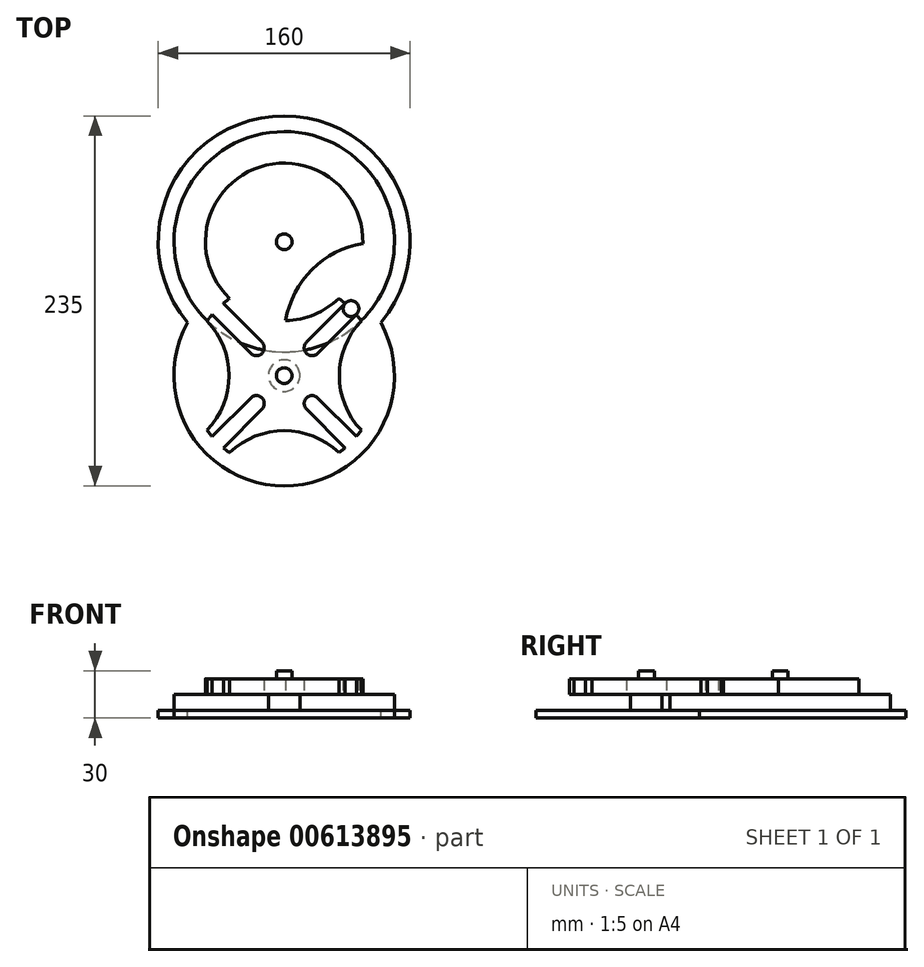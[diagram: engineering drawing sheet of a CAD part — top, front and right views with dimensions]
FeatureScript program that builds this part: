
annotation { "Feature Type Name" : "Feature", "Feature Type Description" : "" }
export const myFeature = defineFeature(function(context is Context, id is Id, definition is map)
    precondition{}
    {
        {
            var Q0;
            Q0=qCreatedBy(makeId("Top.planeOp"),FACE);
            cPlane(context, id + "F0", {"entities" : qUnion([Q0]), "cplaneType" : CPlaneType.OFFSET, "offset" : 10 * mm, "oppositeDirection" : true, "width" : 150 * mm, "height" : 150 * mm});
        }
        {
            var Q0;
            Q0=qCreatedBy(makeId("Top.planeOp"),FACE);
            var sketch = newSketch(context, id + "F1", { "sketchPlane" : qUnion([Q0])});
            skCircle(sketch, "E0", {"center": v(0, 0) * mm, "radius": 70 * mm});
            skCircle(sketch, "E1", {"center": v(0, -60) * mm, "radius": 5 * mm});
            skLineSegment(sketch, "E2", {"start": v(0, -50) * mm, "end": v(0, -70) * mm, "construction": true});
            skCircle(sketch, "E3", {"center": v(0, 0) * mm, "radius": 5 * mm});
            skArc(sketch, "E4", {"start": v(48.84, -50.15) * mm, "mid": v(42.35, -42.5) * mm, "end": v(34.67, -36.03) * mm, "construction": true});
            skArc(sketch, "E5", {"start": v(-48.84, -50.15) * mm, "mid": v(0, -145) * mm, "end": v(48.84, -50.15) * mm, "construction": true});
            skArc(sketch, "E6", {"start": v(-34.67, -36.03) * mm, "mid": v(-42.35, -42.5) * mm, "end": v(-48.84, -50.15) * mm, "construction": true});
            skArc(sketch, "E7", {"start": v(34.67, -36.03) * mm, "mid": v(0, -25) * mm, "end": v(-34.67, -36.03) * mm});
            skArc(sketch, "E8", {"start": v(34.67, -36.03) * mm, "mid": v(0, 50) * mm, "end": v(-34.67, -36.03) * mm});
            skArc(sketch, "E9", {"start": v(-34.67, -36.03) * mm, "mid": v(0, -50) * mm, "end": v(34.67, -36.03) * mm, "construction": true});
            skSolve(sketch);
        }
        {
            var Q0;
            Q0=makeQuery(id+"F1.imprint","IMPRINT",FACE,{"disambiguationData":[TD([[makeQuery(id+"F1.imprint","IMPRINT",EDGE,{"derivedFrom":sQuery(id+"F1.wireOp",EDGE,"E0")}),1.0]])]});
            var Q1;
            Q1=makeQuery(id+"F1.imprint","IMPRINT",FACE,{"disambiguationData":[TD([[makeQuery(id+"F1.imprint","IMPRINT",EDGE,{"derivedFrom":sQuery(id+"F1.wireOp",EDGE,"E3")}),-1.0]])]});
            var Q2;
            Q2=makeQuery(id+"F1.imprint","IMPRINT",FACE,{"disambiguationData":[TD([[makeQuery(id+"F1.imprint","IMPRINT",EDGE,{"derivedFrom":sQuery(id+"F1.wireOp",EDGE,"E1")}),1.0]])]});
            var Q3;
            Q3=qCreatedBy(id+"F0.planeOp",FACE);
            extrude(context, id + "F2", {"entities" : qUnion([Q0, Q1, Q2]), "endBound" : BoundingType.UP_TO_SURFACE, "oppositeDirection" : true, "depth" : 5 * mm, "endBoundEntityFace" : qUnion([Q3]), "offsetDistance" : 25 * mm});
        }
        {
            var Q0;
            Q0=makeQuery(id+"F1.imprint","IMPRINT",FACE,{"disambiguationData":[TD([[makeQuery(id+"F1.imprint","IMPRINT",EDGE,{"derivedFrom":sQuery(id+"F1.wireOp",EDGE,"E3")}),-1.0]])]});
            var Q1;
            Q1=makeQuery(id+"F1.imprint","IMPRINT",FACE,{"disambiguationData":[TD([[makeQuery(id+"F1.imprint","IMPRINT",EDGE,{"derivedFrom":sQuery(id+"F1.wireOp",EDGE,"E1")}),1.0]])]});
            extrude(context, id + "F3", {"entities" : qUnion([Q0, Q1]), "operationType" : NewBodyOperationType.ADD, "depth" : 10 * mm, "offsetDistance" : 25 * mm});
        }
        {
            var Q0;
            Q0=makeQuery(id+"F2.opExtrude","SWEPT_BODY",BODY,{"disambiguationData":[OSD([sQuery(id+"F1.wireOp",EDGE,"E0"),sQuery(id+"F1.wireOp",EDGE,"E3")])]});
            var Q1;
            Q1=makeQuery(id+"F3.opExtrude","CAP_EDGE",EDGE,{"disambiguationData":[OSD([sQuery(id+"F1.wireOp",EDGE,"E3")])],"isStart":false});
            transform(context, id + "F4", {"entities" : qUnion([Q0]), "transformType" : TransformType.ROTATION, "transformAxis" : qUnion([Q1]), "angle" : 45 * degree, "makeCopy" : false});
        }
        {
            var Q0;
            Q0=qCreatedBy(makeId("Top.planeOp"),FACE);
            var sketch = newSketch(context, id + "F5", { "sketchPlane" : qUnion([Q0])});
            skPoint(sketch, "E10.0", {"position": v(0, -85) * mm});
            skLineSegment(sketch, "E11", {"start": v(38.66, -39.12) * mm, "end": v(38.66, -39.12) * mm});
            skArc(sketch, "E12.0", {"start": v(-34.67, -36.03) * mm, "mid": v(0, -50) * mm, "end": v(34.67, -36.03) * mm});
            skLineSegment(sketch, "E13", {"start": v(0, -85) * mm, "end": v(14.14, -70.86) * mm, "construction": true});
            skLineSegment(sketch, "E14", {"start": v(-3.54, -81.46) * mm, "end": v(-42.43, -42.57) * mm, "construction": true});
            skCircle(sketch, "E15.0.0", {"center": v(42.43, -42.43) * mm, "radius": 5 * mm, "construction": true});
            skArc(sketch, "E16", {"start": v(0, -60) * mm, "mid": v(7.2, -61.06) * mm, "end": v(13.8, -64.16) * mm, "construction": true});
            skArc(sketch, "E17", {"start": v(14.13, -63.8) * mm, "mid": v(12.68, -67.33) * mm, "end": v(14.14, -70.86) * mm});
            skLineSegment(sketch, "E18", {"start": v(38.66, -39.12) * mm, "end": v(14.13, -63.8) * mm});
            skArc(sketch, "E19", {"start": v(34.67, -36.03) * mm, "mid": v(-5.07, -25.22) * mm, "end": v(-42.43, -42.57) * mm, "construction": true});
            skArc(sketch, "E20", {"start": v(38.66, -39.12) * mm, "mid": v(36.7, -37.53) * mm, "end": v(34.67, -36.03) * mm});
            skArc(sketch, "E21.MirrorCS", {"start": v(-38.66, -39.12) * mm, "mid": v(-36.7, -37.53) * mm, "end": v(-34.67, -36.03) * mm});
            skLineSegment(sketch, "E22.MirrorCS", {"start": v(0, -85) * mm, "end": v(-14.14, -70.86) * mm, "construction": true});
            skLineSegment(sketch, "E23.MirrorCS", {"start": v(-38.66, -39.12) * mm, "end": v(-14.13, -63.8) * mm});
            skArc(sketch, "E24.MirrorCS", {"start": v(-14.13, -63.8) * mm, "mid": v(-12.68, -67.33) * mm, "end": v(-14.14, -70.86) * mm});
            skArc(sketch, "E25.1.0", {"start": v(-21.2, -70.87) * mm, "mid": v(-17.67, -72.32) * mm, "end": v(-14.14, -70.86) * mm});
            skLineSegment(sketch, "E25.1.1", {"start": v(-45.88, -46.34) * mm, "end": v(-21.2, -70.87) * mm});
            skLineSegment(sketch, "E25.1.2", {"start": v(0, -85) * mm, "end": v(-14.14, -70.86) * mm});
            skArc(sketch, "E25.1.3", {"start": v(-48.97, -119.67) * mm, "mid": v(-35, -85) * mm, "end": v(-48.97, -50.33) * mm});
            skLineSegment(sketch, "E25.1.4", {"start": v(-45.88, -123.66) * mm, "end": v(-21.2, -99.13) * mm});
            skArc(sketch, "E25.1.5", {"start": v(-21.2, -99.13) * mm, "mid": v(-17.67, -97.68) * mm, "end": v(-14.14, -99.14) * mm});
            skLineSegment(sketch, "E25.1.6", {"start": v(0, -85) * mm, "end": v(-14.14, -99.14) * mm, "construction": true});
            skArc(sketch, "E25.1.9", {"start": v(-45.88, -46.34) * mm, "mid": v(-47.47, -48.3) * mm, "end": v(-48.97, -50.33) * mm});
            skArc(sketch, "E25.1.10", {"start": v(-45.88, -123.66) * mm, "mid": v(-47.47, -121.7) * mm, "end": v(-48.97, -119.67) * mm});
            skArc(sketch, "E25.2.0", {"start": v(-14.13, -106.2) * mm, "mid": v(-12.68, -102.67) * mm, "end": v(-14.14, -99.14) * mm});
            skLineSegment(sketch, "E25.2.1", {"start": v(-38.66, -130.88) * mm, "end": v(-14.13, -106.2) * mm});
            skLineSegment(sketch, "E25.2.2", {"start": v(-3.54, -88.54) * mm, "end": v(-14.14, -99.14) * mm});
            skArc(sketch, "E25.2.3", {"start": v(34.67, -133.97) * mm, "mid": v(0, -120) * mm, "end": v(-34.67, -133.97) * mm});
            skLineSegment(sketch, "E25.2.4", {"start": v(38.66, -130.88) * mm, "end": v(14.13, -106.2) * mm});
            skArc(sketch, "E25.2.5", {"start": v(14.13, -106.2) * mm, "mid": v(12.68, -102.67) * mm, "end": v(14.14, -99.14) * mm});
            skLineSegment(sketch, "E25.2.6", {"start": v(0, -85) * mm, "end": v(14.14, -99.14) * mm, "construction": true});
            skArc(sketch, "E25.2.9", {"start": v(-38.66, -130.88) * mm, "mid": v(-36.7, -132.47) * mm, "end": v(-34.67, -133.97) * mm});
            skArc(sketch, "E25.2.10", {"start": v(38.66, -130.88) * mm, "mid": v(36.7, -132.47) * mm, "end": v(34.67, -133.97) * mm});
            skArc(sketch, "E25.3.0", {"start": v(21.2, -99.13) * mm, "mid": v(17.67, -97.68) * mm, "end": v(14.14, -99.14) * mm});
            skLineSegment(sketch, "E25.3.1", {"start": v(45.88, -123.66) * mm, "end": v(21.2, -99.13) * mm});
            skLineSegment(sketch, "E25.3.2", {"start": v(3.54, -88.54) * mm, "end": v(14.14, -99.14) * mm});
            skArc(sketch, "E25.3.3", {"start": v(48.97, -50.33) * mm, "mid": v(35, -85) * mm, "end": v(48.97, -119.67) * mm});
            skLineSegment(sketch, "E25.3.4", {"start": v(45.88, -46.34) * mm, "end": v(21.2, -70.87) * mm});
            skArc(sketch, "E25.3.5", {"start": v(21.2, -70.87) * mm, "mid": v(17.67, -72.32) * mm, "end": v(14.14, -70.86) * mm});
            skLineSegment(sketch, "E25.3.6", {"start": v(3.54, -81.46) * mm, "end": v(14.14, -70.86) * mm});
            skArc(sketch, "E25.3.9", {"start": v(45.88, -123.66) * mm, "mid": v(47.47, -121.7) * mm, "end": v(48.97, -119.67) * mm});
            skArc(sketch, "E25.3.10", {"start": v(45.88, -46.34) * mm, "mid": v(47.47, -48.3) * mm, "end": v(48.97, -50.33) * mm});
            skCircle(sketch, "E26", {"center": v(0, -85) * mm, "radius": 5 * mm});
            skCircle(sketch, "E27", {"center": v(0, -85) * mm, "radius": 10 * mm});
            skSolve(sketch);
        }
        {
            var Q0;
            Q0 = qSketchRegion(id + "F5", true);
            var Q1;
            {var subQ0=sQuery(id+"F5.wireOp",EDGE,"E26");var subQ1=sQuery(id+"F5.wireOp",EDGE,"E25.1.2");var subQ2=makeQuery(id+"F5.imprint","INTERSECT",VERTEX,{"derivedFrom":[subQ1,subQ0]});Q1=makeQuery(id+"F5.imprint","IMPRINT",FACE,{"disambiguationData":[TD([[makeQuery(id+"F5.imprint","IMPRINT",EDGE,{"disambiguationData":[TD([[subQ2,-1.0]])],"derivedFrom":subQ1}),1.0]])]});}
            var Q2;
            {var subQ0=sQuery(id+"F5.wireOp",EDGE,"E26");var subQ1=sQuery(id+"F5.wireOp",EDGE,"E25.1.2");var subQ2=makeQuery(id+"F5.imprint","INTERSECT",VERTEX,{"derivedFrom":[subQ1,subQ0]});Q2=makeQuery(id+"F5.imprint","IMPRINT",FACE,{"disambiguationData":[TD([[makeQuery(id+"F5.imprint","IMPRINT",EDGE,{"disambiguationData":[TD([[subQ2,-1.0]])],"derivedFrom":subQ1}),-1.0]])]});}
            var Q3;
            {var subQ0=sQuery(id+"F5.wireOp",EDGE,"E26");var subQ1=sQuery(id+"F5.wireOp",EDGE,"E25.3.2");var subQ2=makeQuery(id+"F5.imprint","INTERSECT",VERTEX,{"derivedFrom":[subQ1,subQ0]});Q3=makeQuery(id+"F5.imprint","IMPRINT",FACE,{"disambiguationData":[TD([[makeQuery(id+"F5.imprint","IMPRINT",EDGE,{"disambiguationData":[TD([[subQ2,-1.0]])],"derivedFrom":subQ1}),1.0]])]});}
            var Q4;
            {var subQ0=sQuery(id+"F5.wireOp",EDGE,"E26");var subQ1=sQuery(id+"F5.wireOp",EDGE,"E25.2.2");var subQ2=makeQuery(id+"F5.imprint","INTERSECT",VERTEX,{"derivedFrom":[subQ1,subQ0]});Q4=makeQuery(id+"F5.imprint","IMPRINT",FACE,{"disambiguationData":[TD([[makeQuery(id+"F5.imprint","IMPRINT",EDGE,{"disambiguationData":[TD([[subQ2,-1.0]])],"derivedFrom":subQ1}),1.0]])]});}
            extrude(context, id + "F6", {"entities" : qUnion([Q0, Q1, Q2, Q3, Q4]), "depth" : 10 * mm, "offsetDistance" : 25 * mm});
        }
        {
            var Q0;
            {var subQ0=sQuery(id+"F5.wireOp",EDGE,"E26");var subQ1=sQuery(id+"F5.wireOp",EDGE,"E25.3.2");var subQ2=makeQuery(id+"F5.imprint","INTERSECT",VERTEX,{"derivedFrom":[subQ1,subQ0]});Q0=makeQuery(id+"F5.imprint","IMPRINT",FACE,{"disambiguationData":[TD([[makeQuery(id+"F5.imprint","IMPRINT",EDGE,{"disambiguationData":[TD([[subQ2,-1.0]])],"derivedFrom":subQ1}),1.0]])]});}
            var Q1;
            {var subQ0=sQuery(id+"F5.wireOp",EDGE,"E26");var subQ1=sQuery(id+"F5.wireOp",EDGE,"E25.2.2");var subQ2=makeQuery(id+"F5.imprint","INTERSECT",VERTEX,{"derivedFrom":[subQ1,subQ0]});Q1=makeQuery(id+"F5.imprint","IMPRINT",FACE,{"disambiguationData":[TD([[makeQuery(id+"F5.imprint","IMPRINT",EDGE,{"disambiguationData":[TD([[subQ2,-1.0]])],"derivedFrom":subQ1}),1.0]])]});}
            var Q2;
            {var subQ0=sQuery(id+"F5.wireOp",EDGE,"E26");var subQ1=sQuery(id+"F5.wireOp",EDGE,"E25.1.2");var subQ2=makeQuery(id+"F5.imprint","INTERSECT",VERTEX,{"derivedFrom":[subQ1,subQ0]});Q2=makeQuery(id+"F5.imprint","IMPRINT",FACE,{"disambiguationData":[TD([[makeQuery(id+"F5.imprint","IMPRINT",EDGE,{"disambiguationData":[TD([[subQ2,-1.0]])],"derivedFrom":subQ1}),1.0]])]});}
            var Q3;
            {var subQ0=sQuery(id+"F5.wireOp",EDGE,"E26");var subQ1=sQuery(id+"F5.wireOp",EDGE,"E25.1.2");var subQ2=makeQuery(id+"F5.imprint","INTERSECT",VERTEX,{"derivedFrom":[subQ1,subQ0]});Q3=makeQuery(id+"F5.imprint","IMPRINT",FACE,{"disambiguationData":[TD([[makeQuery(id+"F5.imprint","IMPRINT",EDGE,{"disambiguationData":[TD([[subQ2,-1.0]])],"derivedFrom":subQ1}),-1.0]])]});}
            var Q4;
            Q4=qCreatedBy(id+"F0.planeOp",FACE);
            extrude(context, id + "F7", {"entities" : qUnion([Q0, Q1, Q2, Q3]), "operationType" : NewBodyOperationType.ADD, "endBound" : BoundingType.UP_TO_SURFACE, "oppositeDirection" : true, "depth" : 5 * mm, "endBoundEntityFace" : qUnion([Q4]), "offsetDistance" : 25 * mm});
        }
        {
            var Q0;
            Q0=qCreatedBy(id+"F0.planeOp",FACE);
            var sketch = newSketch(context, id + "F8", { "sketchPlane" : qUnion([Q0])});
            skCircle(sketch, "E28.0", {"center": v(0, -85) * mm, "radius": 5 * mm});
            skCircle(sketch, "E29.0", {"center": v(0, 0) * mm, "radius": 5 * mm});
            skArc(sketch, "E30.0", {"start": v(61.37, -51.32) * mm, "mid": v(0, 80) * mm, "end": v(-61.37, -51.32) * mm});
            skArc(sketch, "E31.0", {"start": v(-61.37, -51.32) * mm, "mid": v(0, -155) * mm, "end": v(61.37, -51.32) * mm});
            skSolve(sketch);
        }
        {
            var Q0;
            Q0=makeQuery(id+"F8.imprint","IMPRINT",FACE,{"disambiguationData":[TD([[makeQuery(id+"F8.imprint","IMPRINT",EDGE,{"derivedFrom":sQuery(id+"F8.wireOp",EDGE,"E28.0")}),-1.0]])]});
            var Q1;
            Q1=makeQuery(id+"F8.imprint","IMPRINT",FACE,{"disambiguationData":[TD([[makeQuery(id+"F8.imprint","IMPRINT",EDGE,{"derivedFrom":sQuery(id+"F8.wireOp",EDGE,"E28.0")}),1.0]])]});
            var Q2;
            Q2=makeQuery(id+"F8.imprint","IMPRINT",FACE,{"disambiguationData":[TD([[makeQuery(id+"F8.imprint","IMPRINT",EDGE,{"derivedFrom":sQuery(id+"F8.wireOp",EDGE,"E29.0")}),1.0]])]});
            extrude(context, id + "F9", {"entities" : qUnion([Q0, Q1, Q2]), "oppositeDirection" : true, "depth" : 5 * mm, "offsetDistance" : 25 * mm});
        }
        {
            var Q0;
            Q0=makeQuery(id+"F8.imprint","IMPRINT",FACE,{"disambiguationData":[TD([[makeQuery(id+"F8.imprint","IMPRINT",EDGE,{"derivedFrom":sQuery(id+"F8.wireOp",EDGE,"E29.0")}),1.0]])]});
            var Q1;
            Q1=makeQuery(id+"F8.imprint","IMPRINT",FACE,{"disambiguationData":[TD([[makeQuery(id+"F8.imprint","IMPRINT",EDGE,{"derivedFrom":sQuery(id+"F8.wireOp",EDGE,"E28.0")}),1.0]])]});
            extrude(context, id + "F10", {"entities" : qUnion([Q0, Q1]), "operationType" : NewBodyOperationType.ADD, "depth" : 25 * mm, "offsetDistance" : 25 * mm});
        }
    });
